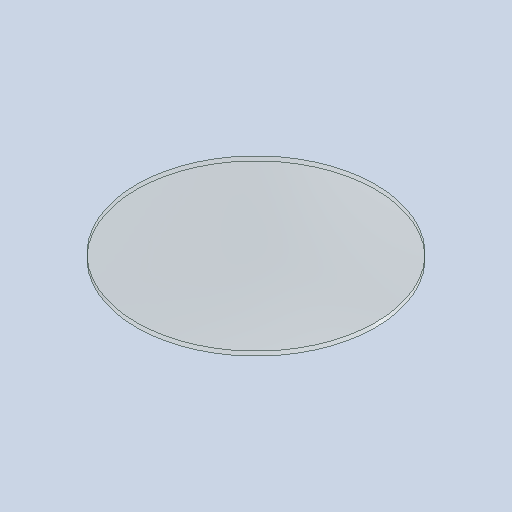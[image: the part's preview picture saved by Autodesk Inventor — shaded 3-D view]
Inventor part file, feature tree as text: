
AUTODESK INVENTOR PART (.ipt)
format: ipt  version: 2025.1 (Build 291241000, 241)  size: 83,968 bytes
history: native  units: mm
features: other x3, sketch x1
ambient origin geometry x8: Origin, YZ Plane, XZ Plane, XY Plane, X Axis, Y Axis, Z Axis, Center Point
bodies: Solid1 (feature_tree)
feature tree (4):
  other  "glass.ipt"
  other  "Solid1::glass.ipt"
  other  "TaggingFeature1"
  sketch  "Sketch1"  dims[d0=10.0mm]
